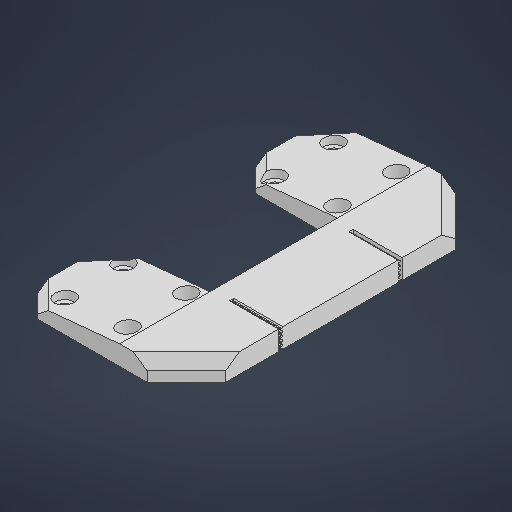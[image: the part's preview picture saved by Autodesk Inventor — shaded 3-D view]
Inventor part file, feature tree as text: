
AUTODESK INVENTOR PART (.ipt)
format: ipt  version: 2025.1 (Build 291241000, 241)  size: 766,976 bytes
history: native  units: mm
features: chamfer x5, sketch x3, extrude x2, projected_geometry x2, pattern_linear x1, hole x1
ambient origin geometry x8: Origin, YZ Plane, XZ Plane, XY Plane, X Axis, Y Axis, Z Axis, Center Point
bodies: Solid1 (feature_tree)
feature tree (14):
  sketch  "Sketch1"  dims[d0=86.0mm d1=157.0mm]
  extrude  "Extrusion1"  Depth=157.0mm
  extrude  "Extrusion2"  Depth=30.0mm
  pattern_linear  "Rectangular Pattern1"  Spacing1=10.0mm  [1 undecoded]
  hole  "Hole3"  [1 undecoded]
  chamfer  "Chamfer1"  Distance=14.0mm
  chamfer  "Chamfer2"  Distance=10.0mm
  chamfer  "Chamfer3"  Distance=52.0mm
  chamfer  "Chamfer4"  Distance=46.0mm
  chamfer  "Chamfer5"  Distance=46.0mm
  sketch  "Sketch2"  dims[d2=32.0mm d3=30.0mm]
  projected_geometry  "Projected Loop1"
  sketch  "Sketch3"  dims[d4=14.0mm d5=10.0mm d6=32.0mm d7=30.0mm d8=10.0mm d9=14.0mm d17=10.0mm d18=0.0mm d36=52.0mm d37=46.0mm d38=46.0mm d39=65.0mm d40=47.0mm d41=47.0mm d49=0.257148mm d50=0.692665mm d51=2.0mm d52=0.25mm d53=1.0mm d60=1.0mm d65=0.55mm d66=0.915725mm d67=25.0mm d68=0.0mm d69=50.0mm d71=2.0mm d72=32.0mm d73=30.0mm d74=32.0mm d75=30.0mm d76=10.0mm d77=10.0mm d78=14.0mm d79=14.0mm d80=5.6mm d81=6.0mm d82=10.0mm d83=8.0mm d84=90.0deg d85=8.0mm d86=20.594885mm d87=20.0mm d88=2.0mm d89=45.0deg d90=10.0mm d91=2.0mm d92=45.0deg d93=5.0mm d94=2.0mm d95=45.0deg d96=52.0mm d97=5.0mm d98=45.0deg d99=4.0mm d100=5.0mm d101=45.0deg]
  projected_geometry  "Projected Loop2"
note: 2 required parameter values undecoded (feature->parameter linkage not recoverable at this tier; creation-order binding heuristic only, values carry confidence <= 0.55)
